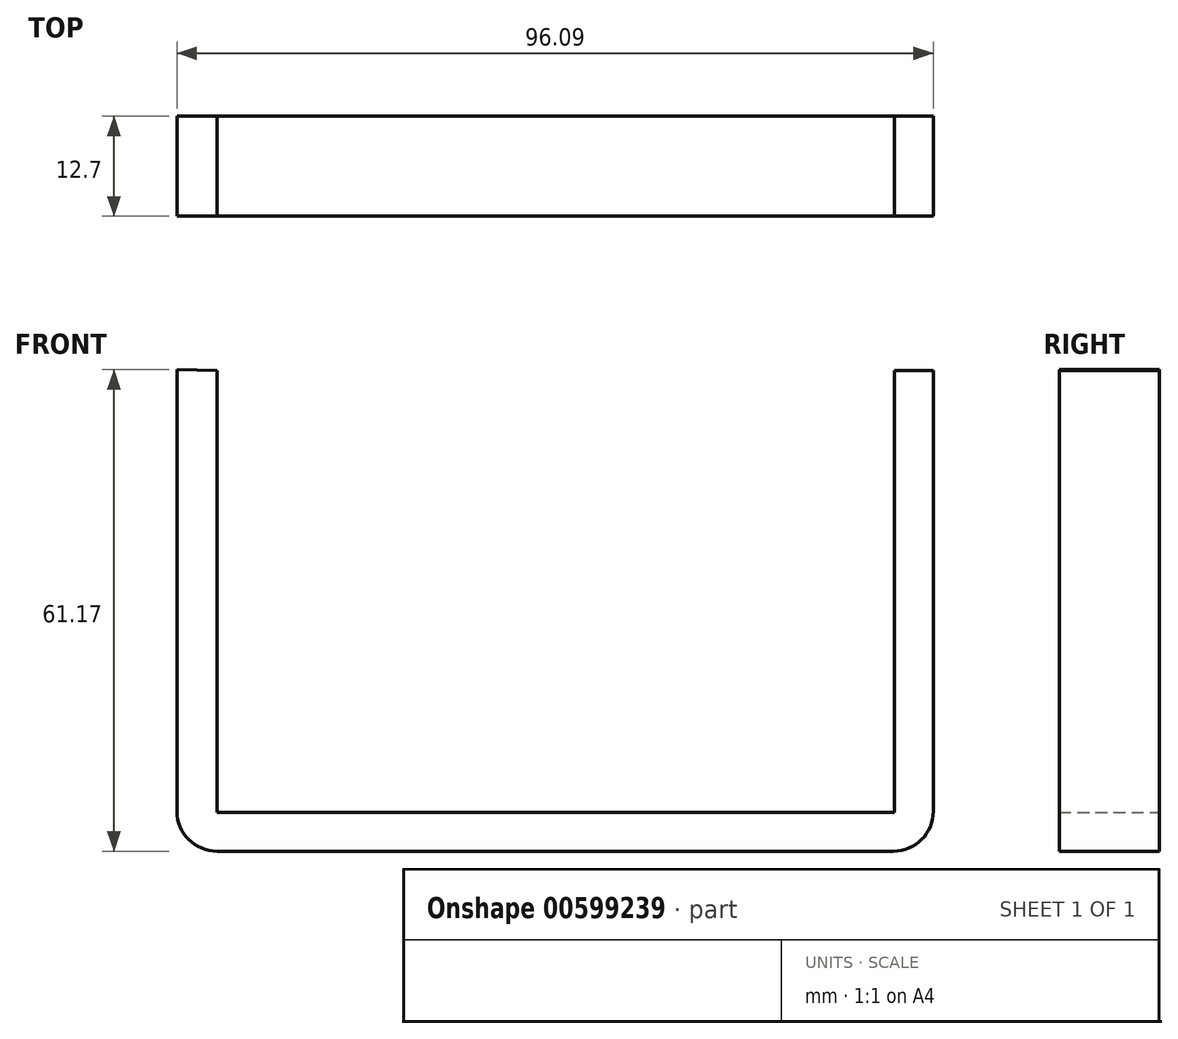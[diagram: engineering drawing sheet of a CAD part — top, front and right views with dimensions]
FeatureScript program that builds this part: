
annotation { "Feature Type Name" : "Feature", "Feature Type Description" : "" }
export const myFeature = defineFeature(function(context is Context, id is Id, definition is map)
    precondition{}
    {
        {
            var Q0;
            Q0=qCreatedBy(makeId("Front.planeOp"),FACE);
            var sketch = newSketch(context, id + "F0", { "sketchPlane" : qUnion([Q0])});
            skLineSegment(sketch, "E0", {"start": v(-55.19, 36.66) * mm, "end": v(-55.19, -24.5) * mm});
            skLineSegment(sketch, "E1", {"start": v(-55.19, -24.5) * mm, "end": v(40.9, -24.5) * mm});
            skLineSegment(sketch, "E2", {"start": v(40.9, -24.5) * mm, "end": v(40.9, 36.59) * mm});
            skLineSegment(sketch, "E3", {"start": v(40.9, 36.59) * mm, "end": v(35.96, 36.59) * mm});
            skLineSegment(sketch, "E4", {"start": v(35.96, 36.59) * mm, "end": v(35.96, -19.58) * mm});
            skLineSegment(sketch, "E5", {"start": v(35.96, -19.58) * mm, "end": v(-50.1, -19.58) * mm});
            skLineSegment(sketch, "E6", {"start": v(-50.1, -19.58) * mm, "end": v(-50.1, 36.59) * mm});
            skLineSegment(sketch, "E7", {"start": v(-50.1, 36.59) * mm, "end": v(-55.19, 36.66) * mm});
            skSolve(sketch);
        }
        {
            var Q0;
            Q0=makeQuery(id+"F0.imprint","IMPRINT",FACE,{"disambiguationData":[TD([[makeQuery(id+"F0.imprint","IMPRINT",EDGE,{"derivedFrom":sQuery(id+"F0.wireOp",EDGE,"E0")}),1.0]])]});
            extrude(context, id + "F1", {"entities" : qUnion([Q0]), "depth" : 12.7 * mm, "offsetDistance" : 25.4 * mm});
        }
        {
            var Q0;
            Q0=makeQuery(id+"F1.opExtrude","SWEPT_EDGE",EDGE,{"disambiguationData":[OSD([sQuery(id+"F0.wireOp",EDGE,"E1"),sQuery(id+"F0.wireOp",EDGE,"E2")])]});
            var Q1;
            Q1=makeQuery(id+"F1.opExtrude","SWEPT_EDGE",EDGE,{"disambiguationData":[OSD([sQuery(id+"F0.wireOp",EDGE,"E0"),sQuery(id+"F0.wireOp",EDGE,"E1")])]});
            fillet(context, id + "F2", {"entities" : qUnion([Q0, Q1]), "radius" : 5.08 * mm, "tangentPropagation" : true, "allowEdgeOverflow" : false});
        }
    });
